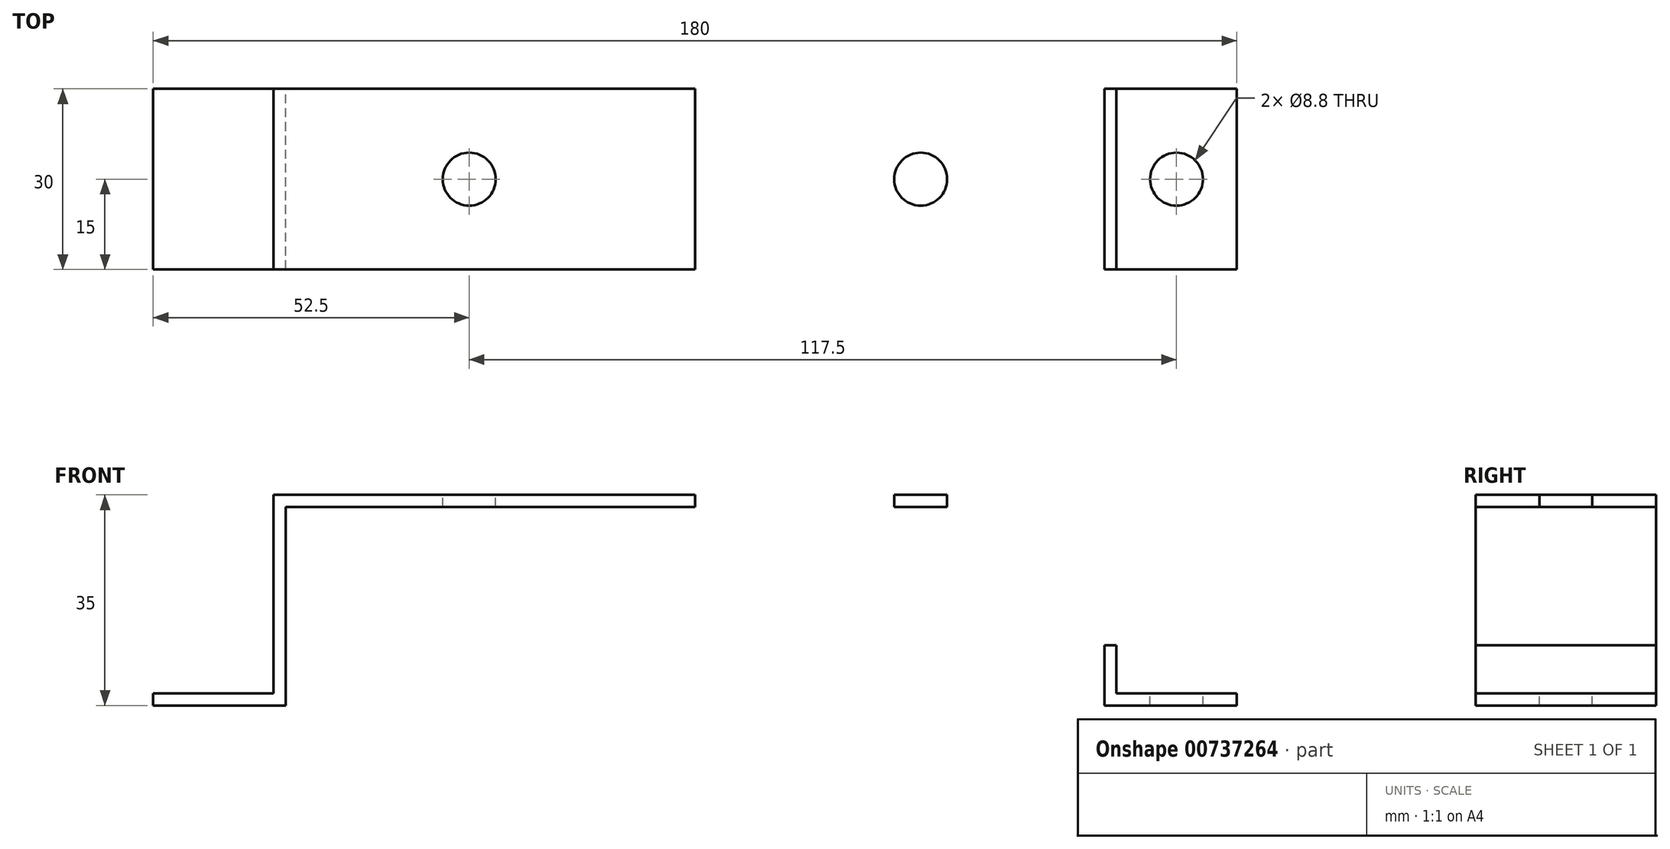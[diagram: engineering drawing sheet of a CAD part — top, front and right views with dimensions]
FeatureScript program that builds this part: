
annotation { "Feature Type Name" : "Feature", "Feature Type Description" : "" }
export const myFeature = defineFeature(function(context is Context, id is Id, definition is map)
    precondition{}
    {
        {
            var Q0;
            Q0=qCreatedBy(makeId("Front.planeOp"),FACE);
            var sketch = newSketch(context, id + "F0", { "sketchPlane" : qUnion([Q0])});
            skLineSegment(sketch, "E0.bottom", {"start": v(90, 1) * mm, "end": v(70, 1) * mm});
            skLineSegment(sketch, "E0.top", {"start": v(90, -1) * mm, "end": v(68, -1) * mm});
            skLineSegment(sketch, "E0.left", {"start": v(90, 1) * mm, "end": v(90, -1) * mm});
            skLineSegment(sketch, "E0.right", {"start": v(-90, 1) * mm, "end": v(-90, -1) * mm});
            skPoint(sketch, "E0.middle", {"position": v(0, 0) * mm});
            skLineSegment(sketch, "E1.top", {"start": v(-70, 34) * mm, "end": v(70, 34) * mm});
            skLineSegment(sketch, "E1.left", {"start": v(-70, 1) * mm, "end": v(-70, 34) * mm});
            skLineSegment(sketch, "E1.right", {"start": v(70, 1) * mm, "end": v(70, 34) * mm});
            skLineSegment(sketch, "E2.0", {"start": v(-68, 32) * mm, "end": v(68, 32) * mm});
            skLineSegment(sketch, "E3.0", {"start": v(-68, -1) * mm, "end": v(-68, 32) * mm});
            skLineSegment(sketch, "E4.0", {"start": v(68, -1) * mm, "end": v(68, 32) * mm});
            skLineSegment(sketch, "E5.trimOffspring", {"start": v(-68, -1) * mm, "end": v(-90, -1) * mm});
            skLineSegment(sketch, "E6.trimOffspring", {"start": v(-70, 1) * mm, "end": v(-90, 1) * mm});
            skPoint(sketch, "E7.orphan", {"position": v(0, 1) * mm});
            skSolve(sketch);
        }
        {
            var Q0;
            Q0=makeQuery(id+"F0.imprint","IMPRINT",FACE,{"disambiguationData":[TD([[makeQuery(id+"F0.imprint","IMPRINT",EDGE,{"derivedFrom":sQuery(id+"F0.wireOp",EDGE,"E0.bottom")}),1.0]])]});
            extrude(context, id + "F1", {"entities" : qUnion([Q0]), "depth" : 30 * mm, "offsetDistance" : 25 * mm});
        }
        {
            var Q0;
            Q0=makeQuery(id+"F1.opExtrude","SWEPT_FACE",FACE,{"disambiguationData":[OSD([sQuery(id+"F0.wireOp",EDGE,"E0.bottom")])]});
            var sketch = newSketch(context, id + "F2", { "sketchPlane" : qUnion([Q0])});
            skCircle(sketch, "E8", {"center": v(80, -15) * mm, "radius": 4.4 * mm});
            skCircle(sketch, "E9.MirrorC", {"center": v(-80, -15) * mm, "radius": 4.4 * mm});
            skSolve(sketch);
        }
        {
            var Q0;
            Q0=makeQuery(id+"F1.opExtrude","SWEPT_FACE",FACE,{"disambiguationData":[OSD([sQuery(id+"F0.wireOp",EDGE,"E1.top")])]});
            var sketch = newSketch(context, id + "F3", { "sketchPlane" : qUnion([Q0])});
            skLineSegment(sketch, "E10", {"start": v(0, 0) * mm, "end": v(0, -30) * mm});
            skCircle(sketch, "E11", {"center": v(-37.5, -15) * mm, "radius": 4.4 * mm});
            skCircle(sketch, "E12.MirrorC", {"center": v(37.5, -15) * mm, "radius": 4.4 * mm});
            skSolve(sketch);
        }
        {
            var Q0;
            Q0=makeQuery(id+"F2.imprint","IMPRINT",FACE,{"disambiguationData":[TD([[makeQuery(id+"F2.imprint","IMPRINT",EDGE,{"derivedFrom":sQuery(id+"F2.wireOp",EDGE,"E9.MirrorC")}),-1.0]])]});
            var Q1;
            Q1=makeQuery(id+"F3.imprint","IMPRINT",FACE,{"disambiguationData":[TD([[makeQuery(id+"F3.imprint","IMPRINT",EDGE,{"derivedFrom":sQuery(id+"F3.wireOp",EDGE,"E11")}),1.0]])]});
            var Q2;
            Q2=makeQuery(id+"F3.imprint","IMPRINT",FACE,{"disambiguationData":[TD([[makeQuery(id+"F3.imprint","IMPRINT",EDGE,{"derivedFrom":sQuery(id+"F3.wireOp",EDGE,"E12.MirrorC")}),-1.0]])]});
            var Q3;
            {var subQ0=sQuery(id+"F2.wireOp",EDGE,"E8");var subQ1=sQuery(id+"F2.wireOp",EDGE,"qyHaVNaX-OBYY-w3NK-5kQH-MvDpQNjSdSPX");var subQ2=makeQuery(id+"F2.imprint","INTERSECT",VERTEX,{"disambiguationData":[OD(0.0)],"derivedFrom":[subQ1,subQ0]});Q3=makeQuery(id+"F2.imprint","IMPRINT",FACE,{"disambiguationData":[TD([[makeQuery(id+"F2.imprint","IMPRINT",EDGE,{"disambiguationData":[TD([[subQ2,-1.0]])],"derivedFrom":subQ1}),-1.0]])]});}
            var Q4;
            {var subQ0=sQuery(id+"F2.wireOp",EDGE,"E8");var subQ1=sQuery(id+"F2.wireOp",EDGE,"qyHaVNaX-OBYY-w3NK-5kQH-MvDpQNjSdSPX");var subQ2=makeQuery(id+"F2.imprint","INTERSECT",VERTEX,{"disambiguationData":[OD(0.0)],"derivedFrom":[subQ1,subQ0]});Q4=makeQuery(id+"F2.imprint","IMPRINT",FACE,{"disambiguationData":[TD([[makeQuery(id+"F2.imprint","IMPRINT",EDGE,{"disambiguationData":[TD([[subQ2,-1.0]])],"derivedFrom":subQ1}),1.0]])]});}
            var Q5;
            Q5=makeQuery(id+"F2.imprint","IMPRINT",FACE,{"disambiguationData":[TD([[makeQuery(id+"F2.imprint","IMPRINT",EDGE,{"derivedFrom":sQuery(id+"F2.wireOp",EDGE,"E8")}),1.0]])]});
            extrude(context, id + "F4", {"entities" : qUnion([Q0, Q1, Q2, Q3, Q4, Q5]), "operationType" : NewBodyOperationType.REMOVE, "oppositeDirection" : true, "depth" : 25 * mm, "offsetDistance" : 25 * mm});
        }
    });
